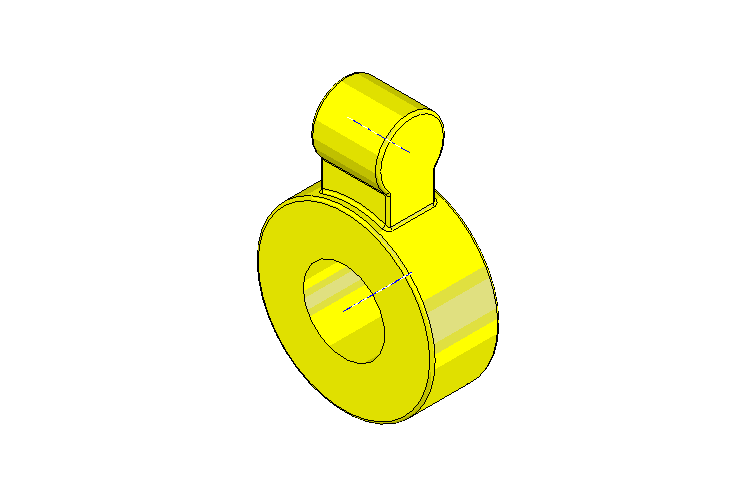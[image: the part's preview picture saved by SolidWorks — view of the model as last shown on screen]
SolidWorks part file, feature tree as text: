
SOLIDWORKS PART (.sldprt)
format: sldprt  version: not decoded by parser v0  size: 148,480 bytes
history: native  units: mm
features: plane x3, sketch x3, extrude x3, material x1, fillet x1 (+10 scaffold rows collapsed)
feature tree (21):
  scaffold x10  (default folders/planes/origin — collapsed)
  material  "Matériau <non spécifié>"
  plane  "Plan de face"
  plane  "Plan de dessus"
  plane  "Plan de droite"
  sketch  "Esquisse1"  dims[D1=6.0mm D2=13.0mm]
  extrude  "Extrusion1"  Depth=5mm
  sketch  "Esquisse2"  dims[D1=5.0mm D2=10.0mm]
  extrude  "Extrusion2"  Depth=5mm
  sketch  "Esquisse3"
  extrude  "Extrusion3"  Depth=3.5mm
  fillet  "Congé1"  Radius=0.2mm
decode coverage: 6 of 7 modeling features carry decoded parameters
note: suppression state not decoded; provenance and decode notes live in map.json
